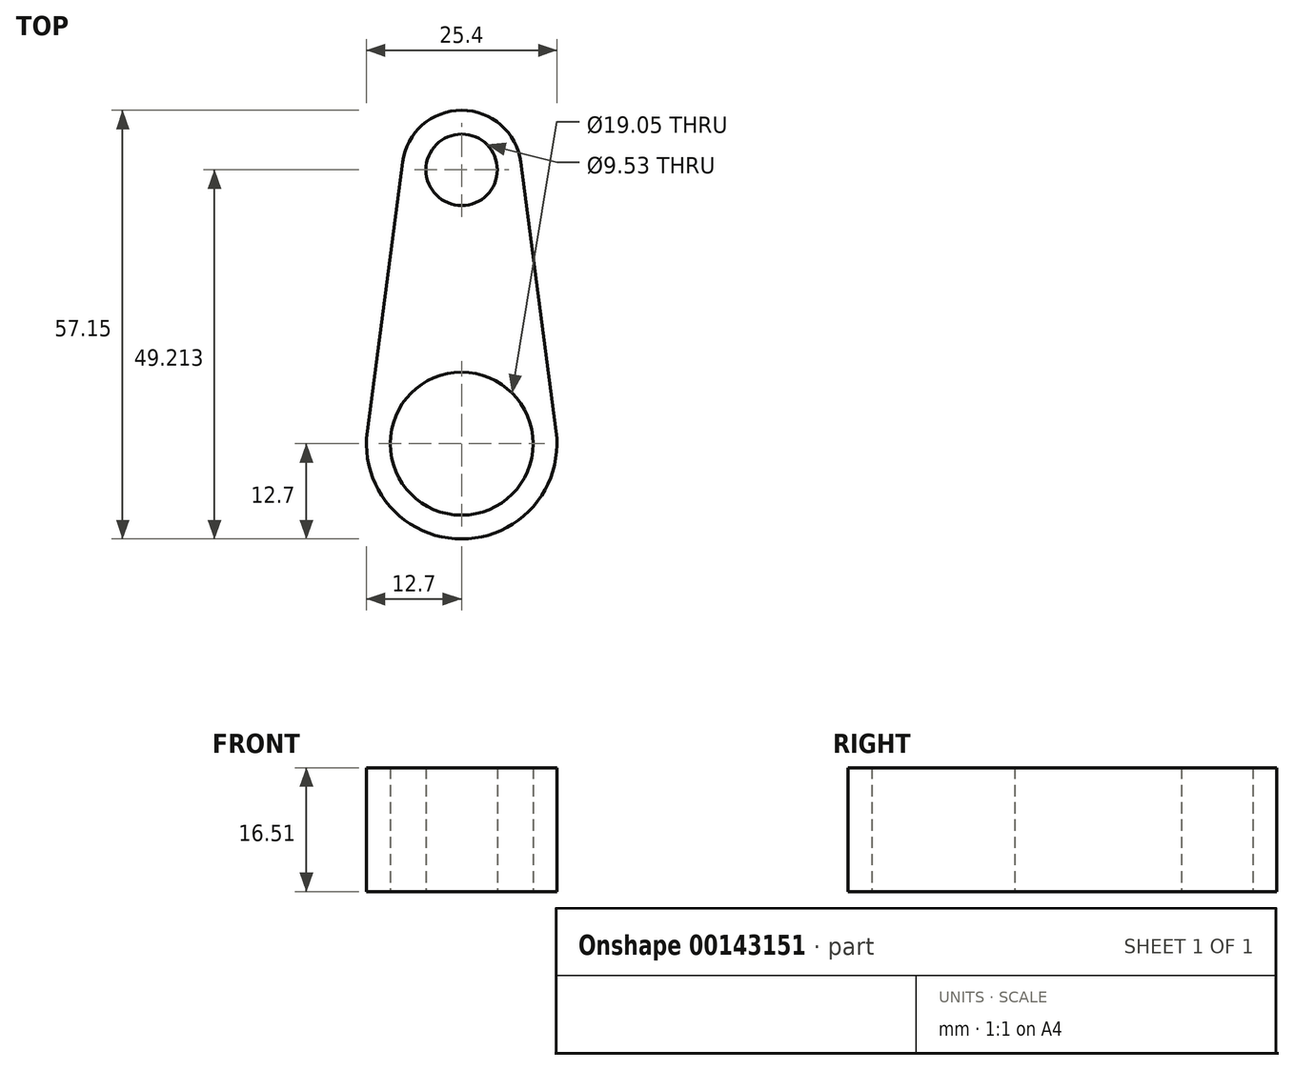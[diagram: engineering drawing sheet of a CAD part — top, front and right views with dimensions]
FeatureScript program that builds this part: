
annotation { "Feature Type Name" : "Feature", "Feature Type Description" : "" }
export const myFeature = defineFeature(function(context is Context, id is Id, definition is map)
    precondition{}
    {
        {
            var Q0;
            Q0=qCreatedBy(makeId("Top.planeOp"),FACE);
            var sketch = newSketch(context, id + "F0", { "sketchPlane" : qUnion([Q0])});
            skCircle(sketch, "E0", {"center": v(0, 0) * mm, "radius": 12.7 * mm});
            skCircle(sketch, "E1", {"center": v(0, 0) * mm, "radius": 9.53 * mm});
            skCircle(sketch, "E2", {"center": v(0, 36.51) * mm, "radius": 7.94 * mm});
            skCircle(sketch, "E3", {"center": v(0, 36.51) * mm, "radius": 4.76 * mm});
            skLineSegment(sketch, "E4", {"start": v(-7.87, 37.55) * mm, "end": v(-12.8, 0) * mm});
            skLineSegment(sketch, "E5", {"start": v(7.87, 37.55) * mm, "end": v(12.6, 1.66) * mm});
            skSolve(sketch);
        }
        {
            var Q0;
            Q0 = qSketchRegion(id + "F0", true);
            extrude(context, id + "F1", {"entities" : qUnion([Q0]), "depth" : 16.5 * mm});
        }
    });
